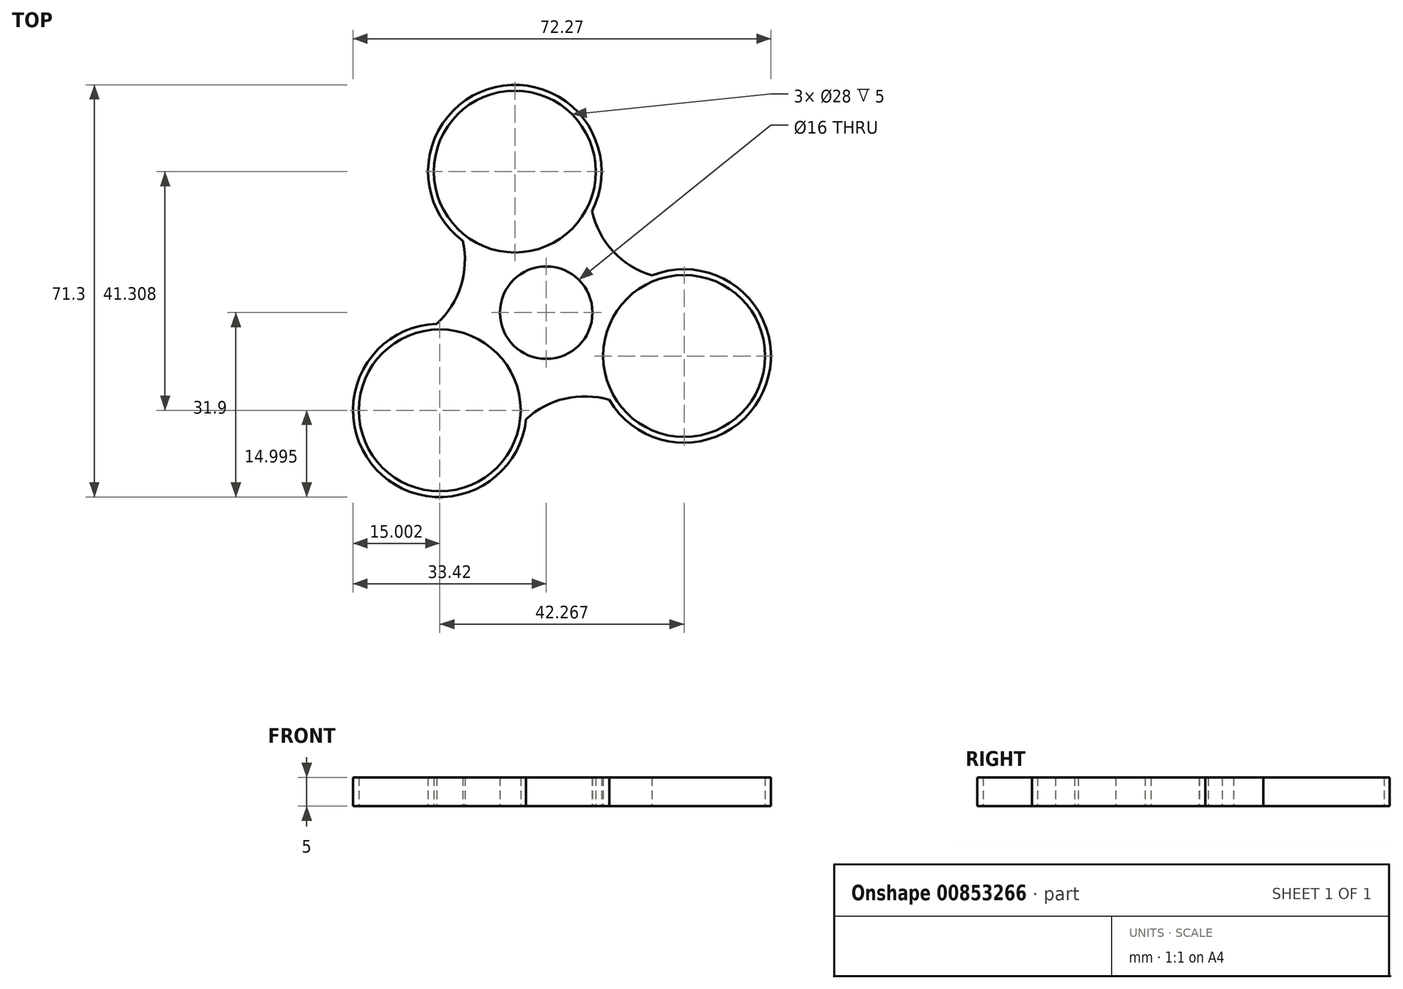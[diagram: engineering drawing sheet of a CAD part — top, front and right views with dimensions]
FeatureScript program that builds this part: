
annotation { "Feature Type Name" : "Feature", "Feature Type Description" : "" }
export const myFeature = defineFeature(function(context is Context, id is Id, definition is map)
    precondition{}
    {
        {
            var Q0;
            Q0=qCreatedBy(makeId("Top.planeOp"),FACE);
            var sketch = newSketch(context, id + "F0", { "sketchPlane" : qUnion([Q0])});
            skCircle(sketch, "E0", {"center": v(0, 0) * mm, "radius": 8 * mm});
            skCircle(sketch, "E1.cCircle", {"center": v(0, 0) * mm, "radius": 10 * mm, "construction": true});
            skLineSegment(sketch, "E1.0", {"start": v(-4.34, 19.52) * mm, "end": v(19.08, -6) * mm, "construction": true});
            skLineSegment(sketch, "E1.1", {"start": v(19.08, -6) * mm, "end": v(-14.73, -13.52) * mm, "construction": true});
            skLineSegment(sketch, "E1.2", {"start": v(-14.73, -13.52) * mm, "end": v(-4.34, 19.52) * mm, "construction": true});
            skPoint(sketch, "E1.0.midPoint", {"position": v(7.37, 6.76) * mm});
            skLineSegment(sketch, "E2", {"start": v(0, 0) * mm, "end": v(-9.6, 43.12) * mm, "construction": true});
            skLineSegment(sketch, "E3", {"start": v(0, 0) * mm, "end": v(53.7, -16.88) * mm, "construction": true});
            skLineSegment(sketch, "E4", {"start": v(0, 0) * mm, "end": v(-29.05, -26.67) * mm, "construction": true});
            skCircle(sketch, "E5", {"center": v(-5.43, 24.4) * mm, "radius": 15 * mm});
            skCircle(sketch, "E6", {"center": v(23.85, -7.5) * mm, "radius": 15 * mm});
            skCircle(sketch, "E7", {"center": v(-18.42, -16.9) * mm, "radius": 15 * mm});
            skLineSegment(sketch, "E8", {"start": v(-5.43, 24.4) * mm, "end": v(14.72, 28.89) * mm, "construction": true});
            skLineSegment(sketch, "E9", {"start": v(14.72, 28.89) * mm, "end": v(-26.3, 19.76) * mm, "construction": true});
            skLineSegment(sketch, "E10", {"start": v(-18.42, -16.9) * mm, "end": v(-38.8, 5.3) * mm, "construction": true});
            skLineSegment(sketch, "E11", {"start": v(-38.8, 5.3) * mm, "end": v(-1.77, -35.05) * mm, "construction": true});
            skLineSegment(sketch, "E12", {"start": v(23.85, -7.5) * mm, "end": v(30.7, 15.55) * mm, "construction": true});
            skLineSegment(sketch, "E13", {"start": v(30.7, 15.55) * mm, "end": v(16.82, -31.15) * mm, "construction": true});
            skArc(sketch, "E14", {"start": v(9.21, 27.66) * mm, "mid": v(11.46, 10.71) * mm, "end": v(28.12, 6.88) * mm});
            skArc(sketch, "E15", {"start": v(-28.56, -5.85) * mm, "mid": v(-14.75, 4.64) * mm, "end": v(-20.07, 21.14) * mm});
            skArc(sketch, "E16", {"start": v(19.58, -21.88) * mm, "mid": v(3.45, -14.83) * mm, "end": v(-8.28, -27.96) * mm});
            skCircle(sketch, "E17", {"center": v(-5.43, 24.4) * mm, "radius": 14 * mm});
            skCircle(sketch, "E18", {"center": v(23.85, -7.5) * mm, "radius": 14 * mm});
            skCircle(sketch, "E19", {"center": v(-18.42, -16.9) * mm, "radius": 14 * mm});
            skSolve(sketch);
        }
        {
            var Q0;
            {var subQ5=sQuery(id+"F0.wireOp",EDGE,"E6");var subQ6=makeQuery(id+"F0.imprint","INTERSECT",VERTEX,{"derivedFrom":[subQ5,sQuery(id+"F0.wireOp",EDGE,"M7z9cIOD-1KO4-ufdf-UPls-Mq20f6Fcb5sd")]});Q0=makeQuery(id+"F0.imprint","IMPRINT",FACE,{"disambiguationData":[TD([[makeQuery(id+"F0.imprint","IMPRINT",EDGE,{"disambiguationData":[TD([[subQ6,1.0]])],"derivedFrom":subQ5}),1.0]])]});}
            var Q1;
            {var subQ0=sQuery(id+"F0.wireOp",EDGE,"Rj7F02r8-Ud2X-WsfZ-kHEN-uf11etLTQIcZ");Q1=makeQuery(id+"F0.imprint","IMPRINT",FACE,{"disambiguationData":[TD([[makeQuery(id+"F0.imprint","IMPRINT",EDGE,{"derivedFrom":subQ0}),1.0]])]});}
            var Q2;
            {var subQ0=sQuery(id+"F0.wireOp",EDGE,"E14");var subQ1=sQuery(id+"F0.wireOp",EDGE,"E6");var subQ2=makeQuery(id+"F0.imprint","INTERSECT",VERTEX,{"disambiguationData":[OD(0.0)],"derivedFrom":[subQ1,subQ0]});Q2=makeQuery(id+"F0.imprint","IMPRINT",FACE,{"disambiguationData":[TD([[makeQuery(id+"F0.imprint","IMPRINT",EDGE,{"disambiguationData":[TD([[subQ2,-1.0]])],"derivedFrom":subQ1}),1.0]])]});}
            var Q3;
            {var subQ1=sQuery(id+"F0.wireOp",EDGE,"E6");var subQ3=sQuery(id+"F0.wireOp",EDGE,"ygeVa6C7-mJnH-QFzG-bxIm-BiXJWj1OISzp");var subQ4=makeQuery(id+"F0.imprint","INTERSECT",VERTEX,{"derivedFrom":[subQ1,subQ3]});Q3=makeQuery(id+"F0.imprint","IMPRINT",FACE,{"disambiguationData":[TD([[makeQuery(id+"F0.imprint","IMPRINT",EDGE,{"disambiguationData":[TD([[subQ4,-1.0]])],"derivedFrom":subQ3}),1.0]])]});}
            var Q4;
            {var subQ3=sQuery(id+"F0.wireOp",EDGE,"E14");var subQ6=sQuery(id+"F0.wireOp",EDGE,"E6");var subQ8=makeQuery(id+"F0.imprint","INTERSECT",VERTEX,{"disambiguationData":[OD(1.0)],"derivedFrom":[subQ6,subQ3]});Q4=makeQuery(id+"F0.imprint","IMPRINT",FACE,{"disambiguationData":[TD([[makeQuery(id+"F0.imprint","IMPRINT",EDGE,{"disambiguationData":[TD([[subQ8,-1.0]])],"derivedFrom":subQ3}),-1.0]])]});}
            var Q5;
            {var subQ1=sQuery(id+"F0.wireOp",EDGE,"OofhiGZP-RtBi-PtYZ-0z5y-P3M5ZNXA8OdQ");Q5=makeQuery(id+"F0.imprint","IMPRINT",FACE,{"disambiguationData":[TD([[makeQuery(id+"F0.imprint","IMPRINT",EDGE,{"derivedFrom":subQ1}),1.0]])]});}
            var Q6;
            {var subQ1=sQuery(id+"F0.wireOp",EDGE,"E5");var subQ3=sQuery(id+"F0.wireOp",EDGE,"omfQdX7M-Q9sV-O8Hz-vPT6-XyIvn6SMrGQv");var subQ4=makeQuery(id+"F0.imprint","INTERSECT",VERTEX,{"derivedFrom":[subQ1,subQ3]});Q6=makeQuery(id+"F0.imprint","IMPRINT",FACE,{"disambiguationData":[TD([[makeQuery(id+"F0.imprint","IMPRINT",EDGE,{"disambiguationData":[TD([[subQ4,-1.0]])],"derivedFrom":subQ3}),1.0]])]});}
            var Q7;
            {var subQ3=sQuery(id+"F0.wireOp",EDGE,"E15");var subQ6=sQuery(id+"F0.wireOp",EDGE,"E5");var subQ8=makeQuery(id+"F0.imprint","INTERSECT",VERTEX,{"disambiguationData":[OD(1.0)],"derivedFrom":[subQ6,subQ3]});Q7=makeQuery(id+"F0.imprint","IMPRINT",FACE,{"disambiguationData":[TD([[makeQuery(id+"F0.imprint","IMPRINT",EDGE,{"disambiguationData":[TD([[subQ8,-1.0]])],"derivedFrom":subQ3}),-1.0]])]});}
            var Q8;
            {var subQ1=sQuery(id+"F0.wireOp",EDGE,"E5");var subQ3=makeQuery(id+"F0.imprint","INTERSECT",VERTEX,{"derivedFrom":[subQ1,sQuery(id+"F0.wireOp",EDGE,"NNF1IXcO-KDtx-LrZy-GyvK-SdWHQc5rbq9X")]});Q8=makeQuery(id+"F0.imprint","IMPRINT",FACE,{"disambiguationData":[TD([[makeQuery(id+"F0.imprint","IMPRINT",EDGE,{"disambiguationData":[TD([[subQ3,1.0]])],"derivedFrom":subQ1}),1.0]])]});}
            var Q9;
            {var subQ0=sQuery(id+"F0.wireOp",EDGE,"E15");var subQ1=sQuery(id+"F0.wireOp",EDGE,"E5");var subQ2=makeQuery(id+"F0.imprint","INTERSECT",VERTEX,{"disambiguationData":[OD(0.0)],"derivedFrom":[subQ1,subQ0]});Q9=makeQuery(id+"F0.imprint","IMPRINT",FACE,{"disambiguationData":[TD([[makeQuery(id+"F0.imprint","IMPRINT",EDGE,{"disambiguationData":[TD([[subQ2,-1.0]])],"derivedFrom":subQ1}),1.0]])]});}
            var Q10;
            {var subQ0=sQuery(id+"F0.wireOp",EDGE,"E16");var subQ1=sQuery(id+"F0.wireOp",EDGE,"E7");var subQ2=makeQuery(id+"F0.imprint","INTERSECT",VERTEX,{"disambiguationData":[OD(0.0)],"derivedFrom":[subQ1,subQ0]});Q10=makeQuery(id+"F0.imprint","IMPRINT",FACE,{"disambiguationData":[TD([[makeQuery(id+"F0.imprint","IMPRINT",EDGE,{"disambiguationData":[TD([[subQ2,-1.0]])],"derivedFrom":subQ1}),1.0]])]});}
            var Q11;
            {var subQ5=sQuery(id+"F0.wireOp",EDGE,"E7");var subQ7=makeQuery(id+"F0.imprint","INTERSECT",VERTEX,{"derivedFrom":[subQ5,sQuery(id+"F0.wireOp",EDGE,"r51XLC6Q-39pv-j4Mh-tc2X-xKCWA9CAiyjs")]});Q11=makeQuery(id+"F0.imprint","IMPRINT",FACE,{"disambiguationData":[TD([[makeQuery(id+"F0.imprint","IMPRINT",EDGE,{"disambiguationData":[TD([[subQ7,1.0]])],"derivedFrom":subQ5}),1.0]])]});}
            var Q12;
            {var subQ1=sQuery(id+"F0.wireOp",EDGE,"GRHSHT9T-QICB-gy7Z-1OSC-em1TjoAzbnqL");Q12=makeQuery(id+"F0.imprint","IMPRINT",FACE,{"disambiguationData":[TD([[makeQuery(id+"F0.imprint","IMPRINT",EDGE,{"derivedFrom":subQ1}),1.0]])]});}
            var Q13;
            {var subQ1=sQuery(id+"F0.wireOp",EDGE,"E7");var subQ3=sQuery(id+"F0.wireOp",EDGE,"0lfD7g5A-rLUq-UXtI-SeMV-Qkrn6wi8wpPh");var subQ4=makeQuery(id+"F0.imprint","INTERSECT",VERTEX,{"derivedFrom":[subQ1,subQ3]});Q13=makeQuery(id+"F0.imprint","IMPRINT",FACE,{"disambiguationData":[TD([[makeQuery(id+"F0.imprint","IMPRINT",EDGE,{"disambiguationData":[TD([[subQ4,-1.0]])],"derivedFrom":subQ3}),1.0]])]});}
            var Q14;
            {var subQ3=sQuery(id+"F0.wireOp",EDGE,"E16");var subQ5=sQuery(id+"F0.wireOp",EDGE,"E7");var subQ6=makeQuery(id+"F0.imprint","INTERSECT",VERTEX,{"disambiguationData":[OD(1.0)],"derivedFrom":[subQ5,subQ3]});Q14=makeQuery(id+"F0.imprint","IMPRINT",FACE,{"disambiguationData":[TD([[makeQuery(id+"F0.imprint","IMPRINT",EDGE,{"disambiguationData":[TD([[subQ6,-1.0]])],"derivedFrom":subQ3}),-1.0]])]});}
            var Q15;
            Q15=makeQuery(id+"F0.imprint","IMPRINT",FACE,{"disambiguationData":[TD([[makeQuery(id+"F0.imprint","IMPRINT",EDGE,{"derivedFrom":sQuery(id+"F0.wireOp",EDGE,"E0")}),-1.0]])]});
            extrude(context, id + "F1", {"entities" : qUnion([Q0, Q1, Q2, Q3, Q4, Q5, Q6, Q7, Q8, Q9, Q10, Q11, Q12, Q13, Q14, Q15]), "depth" : 5 * mm, "offsetDistance" : 25 * mm});
        }
    });
